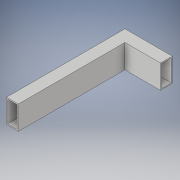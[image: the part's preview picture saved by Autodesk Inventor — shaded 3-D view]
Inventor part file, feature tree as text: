
AUTODESK INVENTOR PART (.ipt)
format: ipt  version: 2018 (Build 220112000, 112)  size: 133,120 bytes
history: native  units: in
note: dims shown in document units (in); Inventor stores cm internally (conversion verified against a paired STEP export)
features: extrude x3, sketch x3
ambient origin geometry x8: Origin, YZ Plane, XZ Plane, XY Plane, X Axis, Y Axis, Z Axis, Center Point
bodies: Body1 (feature_tree)
feature tree (6):
  extrude  "Extrusion12"  Depth=2.0in
  extrude  "Extrusion14"  Depth=0.1in
  extrude  "Extrusion16"  Depth=0.1in
  sketch  "Sketch15"  dims[d46=1.0in d47=2.0in]
  sketch  "Sketch17"  dims[d48=0.1in d49=0.1in]
  sketch  "Sketch20"  dims[d50=0.1in d51=0.1in d52=3.0in d53=0.0in d62=0.1in d63=0.0in d71=1.0in d72=2.0in d73=0.1in d74=0.1in d75=0.1in d76=0.1in d77=0.1in d78=0.0in d79=10.0in d80=0.0in]
